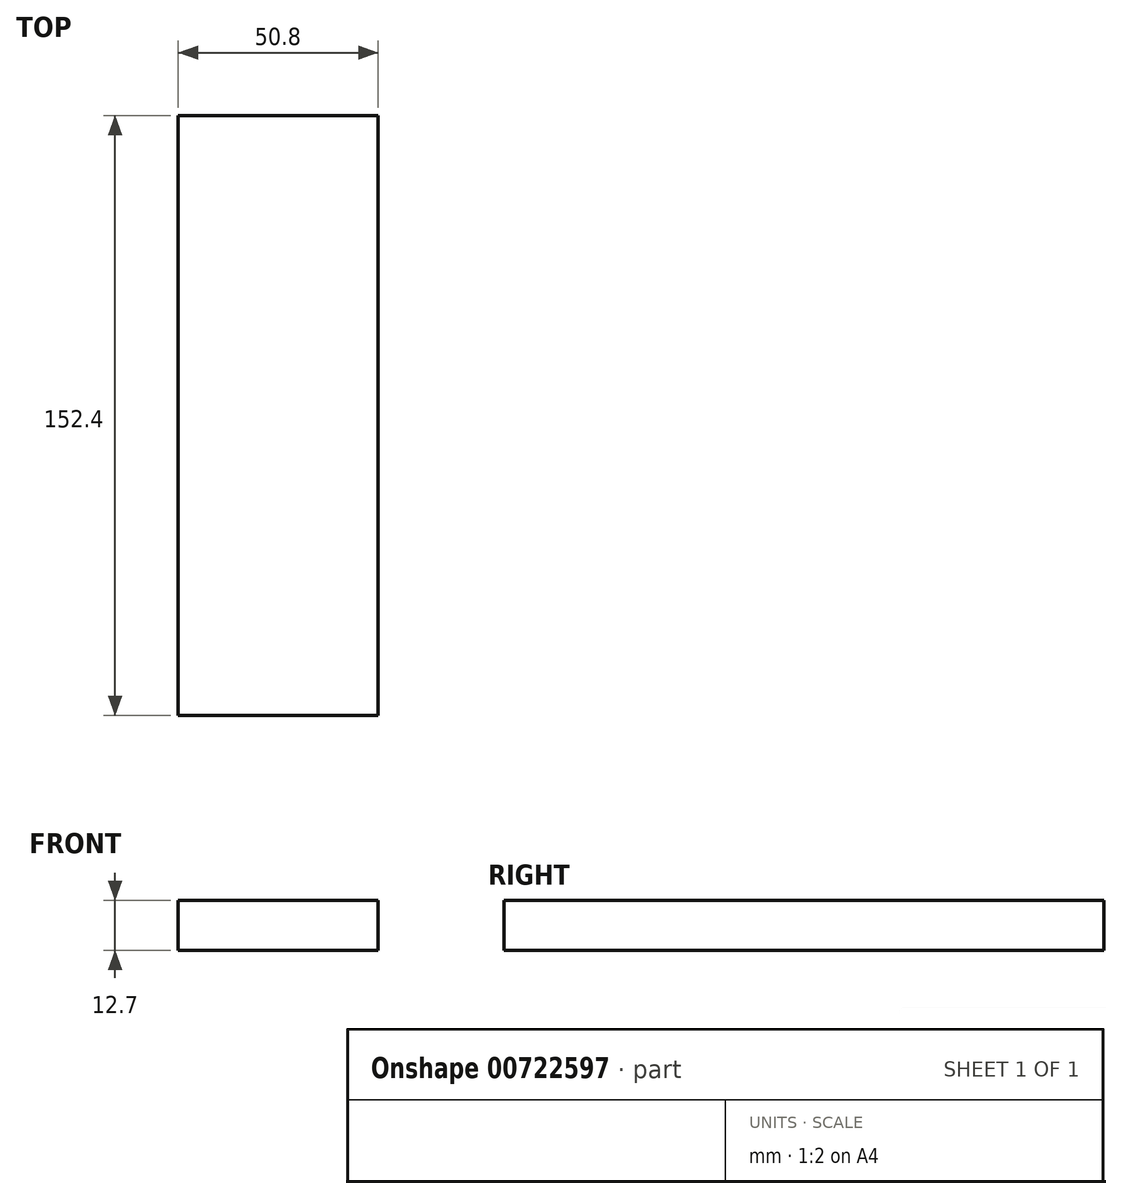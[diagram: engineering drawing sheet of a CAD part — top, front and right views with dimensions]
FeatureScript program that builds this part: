
annotation { "Feature Type Name" : "Feature", "Feature Type Description" : "" }
export const myFeature = defineFeature(function(context is Context, id is Id, definition is map)
    precondition{}
    {
        {
            var Q0;
            Q0=qCreatedBy(makeId("Top.planeOp"),FACE);
            var sketch = newSketch(context, id + "F0", { "sketchPlane" : qUnion([Q0])});
            skLineSegment(sketch, "E0.bottom", {"start": v(-25.4, -76.2) * mm, "end": v(25.4, -76.2) * mm});
            skLineSegment(sketch, "E0.top", {"start": v(-25.4, 76.2) * mm, "end": v(25.4, 76.2) * mm});
            skLineSegment(sketch, "E0.left", {"start": v(-25.4, -76.2) * mm, "end": v(-25.4, 76.2) * mm});
            skLineSegment(sketch, "E0.right", {"start": v(25.4, -76.2) * mm, "end": v(25.4, 76.2) * mm});
            skPoint(sketch, "E0.middle", {"position": v(0, 0) * mm});
            skSolve(sketch);
        }
        {
            var Q0;
            Q0=makeQuery(id+"F0.imprint","IMPRINT",FACE,{"disambiguationData":[TD([[makeQuery(id+"F0.imprint","IMPRINT",EDGE,{"derivedFrom":sQuery(id+"F0.wireOp",EDGE,"E0.bottom")}),1.0]])]});
            extrude(context, id + "F1", {"entities" : qUnion([Q0]), "endBound" : BoundingType.SYMMETRIC, "depth" : 12.7 * mm, "offsetDistance" : 25 * mm});
        }
    });
